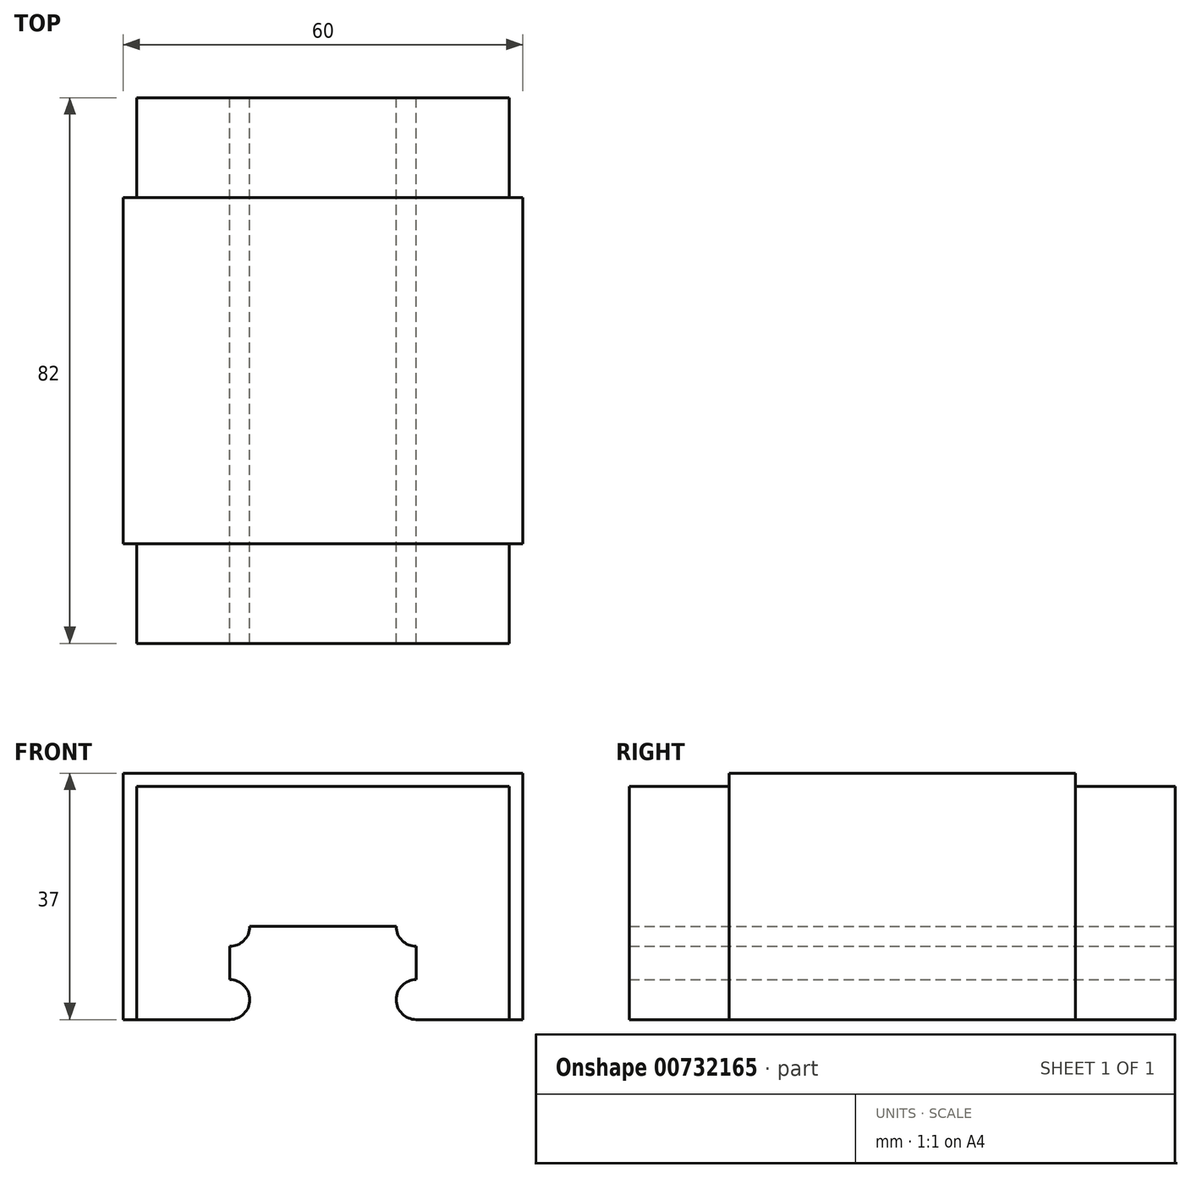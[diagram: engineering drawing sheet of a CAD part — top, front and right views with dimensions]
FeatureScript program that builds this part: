
annotation { "Feature Type Name" : "Feature", "Feature Type Description" : "" }
export const myFeature = defineFeature(function(context is Context, id is Id, definition is map)
    precondition{}
    {
        {
            var Q0;
            Q0=qCreatedBy(makeId("Front.planeOp"),FACE);
            var sketch = newSketch(context, id + "F0", { "sketchPlane" : qUnion([Q0])});
            skLineSegment(sketch, "E0", {"start": v(19, 14) * mm, "end": v(41, 14) * mm});
            skLineSegment(sketch, "E1", {"start": v(44, 11) * mm, "end": v(44, 6) * mm});
            skArc(sketch, "E2", {"start": v(16, 0) * mm, "mid": v(19, 3) * mm, "end": v(16, 6) * mm});
            skArc(sketch, "E3", {"start": v(44, 6) * mm, "mid": v(41, 3) * mm, "end": v(44, 0) * mm});
            skLineSegment(sketch, "E4.trimOffspring", {"start": v(16, 6) * mm, "end": v(16, 11) * mm});
            skArc(sketch, "E5", {"start": v(16, 11) * mm, "mid": v(18.12, 11.88) * mm, "end": v(19, 14) * mm});
            skArc(sketch, "E6", {"start": v(41, 14) * mm, "mid": v(41.88, 11.88) * mm, "end": v(44, 11) * mm});
            skLineSegment(sketch, "E7", {"start": v(16, 0) * mm, "end": v(0, 0) * mm});
            skLineSegment(sketch, "E8", {"start": v(0, 0) * mm, "end": v(0, 37) * mm});
            skLineSegment(sketch, "E9", {"start": v(0, 37) * mm, "end": v(60, 37) * mm});
            skLineSegment(sketch, "E10", {"start": v(60, 37) * mm, "end": v(60, 0) * mm});
            skLineSegment(sketch, "E11", {"start": v(60, 0) * mm, "end": v(44, 0) * mm});
            skSolve(sketch);
        }
        {
            var Q0;
            Q0=qSketchRegion(id+"F0",true);
            extrude(context, id + "F1", {"entities" : qUnion([Q0]), "depth" : 82 * mm});
        }
        {
            var Q0;
            Q0=makeQuery(id+"F1.opExtrude","SWEPT_FACE",FACE,{"disambiguationData":[OSD([sQuery(id+"F0.wireOp",EDGE,"E9")])]});
            var sketch = newSketch(context, id + "F2", { "sketchPlane" : qUnion([Q0])});
            skLineSegment(sketch, "E12.bottom", {"start": v(0, 0) * mm, "end": v(60, 0) * mm});
            skLineSegment(sketch, "E12.top", {"start": v(0, -15) * mm, "end": v(60, -15) * mm});
            skLineSegment(sketch, "E12.left", {"start": v(0, 0) * mm, "end": v(0, -15) * mm});
            skLineSegment(sketch, "E12.right", {"start": v(60, 0) * mm, "end": v(60, -15) * mm});
            skLineSegment(sketch, "E13.bottom", {"start": v(0, -82) * mm, "end": v(60, -82) * mm});
            skLineSegment(sketch, "E13.top", {"start": v(0, -67) * mm, "end": v(60, -67) * mm});
            skLineSegment(sketch, "E13.left", {"start": v(0, -82) * mm, "end": v(0, -67) * mm});
            skLineSegment(sketch, "E13.right", {"start": v(60, -82) * mm, "end": v(60, -67) * mm});
            skSolve(sketch);
        }
        {
            var Q0;
            Q0=qSketchRegion(id+"F2",true);
            extrude(context, id + "F3", {"entities" : qUnion([Q0]), "operationType" : NewBodyOperationType.REMOVE, "oppositeDirection" : true, "depth" : 2 * mm});
        }
        {
            var Q0;
            Q0=makeQuery(id+"F3.boolean.opBoolean","COPY",FACE,{"derivedFrom":makeQuery(id+"F3.opExtrude","CAP_FACE",FACE,{"disambiguationData":[OSD([sQuery(id+"F2.wireOp",EDGE,"E12.bottom"),sQuery(id+"F2.wireOp",EDGE,"E12.top"),sQuery(id+"F2.wireOp",EDGE,"E12.left"),sQuery(id+"F2.wireOp",EDGE,"E12.right")])],"isStart":false})});
            var sketch = newSketch(context, id + "F4", { "sketchPlane" : qUnion([Q0])});
            skLineSegment(sketch, "E14.bottom", {"start": v(0, 0) * mm, "end": v(2, 0) * mm});
            skLineSegment(sketch, "E14.top", {"start": v(0, -15) * mm, "end": v(2, -15) * mm});
            skLineSegment(sketch, "E14.left", {"start": v(0, 0) * mm, "end": v(0, -15) * mm});
            skLineSegment(sketch, "E14.right", {"start": v(2, 0) * mm, "end": v(2, -15) * mm});
            skLineSegment(sketch, "E15.bottom", {"start": v(60, 0) * mm, "end": v(58, 0) * mm});
            skLineSegment(sketch, "E15.top", {"start": v(60, -15) * mm, "end": v(58, -15) * mm});
            skLineSegment(sketch, "E15.left", {"start": v(60, 0) * mm, "end": v(60, -15) * mm});
            skLineSegment(sketch, "E15.right", {"start": v(58, 0) * mm, "end": v(58, -15) * mm});
            skLineSegment(sketch, "E16.bottom", {"start": v(0, -67) * mm, "end": v(2, -67) * mm});
            skLineSegment(sketch, "E16.top", {"start": v(0, -82) * mm, "end": v(2, -82) * mm});
            skLineSegment(sketch, "E16.left", {"start": v(0, -67) * mm, "end": v(0, -82) * mm});
            skLineSegment(sketch, "E16.right", {"start": v(2, -67) * mm, "end": v(2, -82) * mm});
            skLineSegment(sketch, "E17.bottom", {"start": v(60, -82) * mm, "end": v(58, -82) * mm});
            skLineSegment(sketch, "E17.top", {"start": v(60, -67) * mm, "end": v(58, -67) * mm});
            skLineSegment(sketch, "E17.left", {"start": v(60, -82) * mm, "end": v(60, -67) * mm});
            skLineSegment(sketch, "E17.right", {"start": v(58, -82) * mm, "end": v(58, -67) * mm});
            skSolve(sketch);
        }
        {
            var Q0;
            Q0=qSketchRegion(id+"F4",true);
            extrude(context, id + "F5", {"entities" : qUnion([Q0]), "operationType" : NewBodyOperationType.REMOVE, "oppositeDirection" : true, "depth" : 35 * mm});
        }
    });
